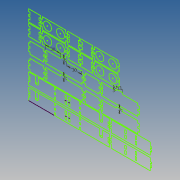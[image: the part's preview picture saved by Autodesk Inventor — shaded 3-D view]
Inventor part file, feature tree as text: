
AUTODESK INVENTOR PART (.ipt)
format: ipt  version: 2020 (Build 240168000, 168)  size: 247,808 bytes
history: native  units: mm
features: sketch x1
ambient origin geometry x8: Origin, YZ Plane, XZ Plane, XY Plane, X Axis, Y Axis, Z Axis, Center Point
feature tree (1):
  sketch  "Sketch1"  dims[d130=30.0mm d131=30.0mm d132=3.0mm d136=3.0mm d137=3.0mm d138=3.0mm d139=13.0mm]
